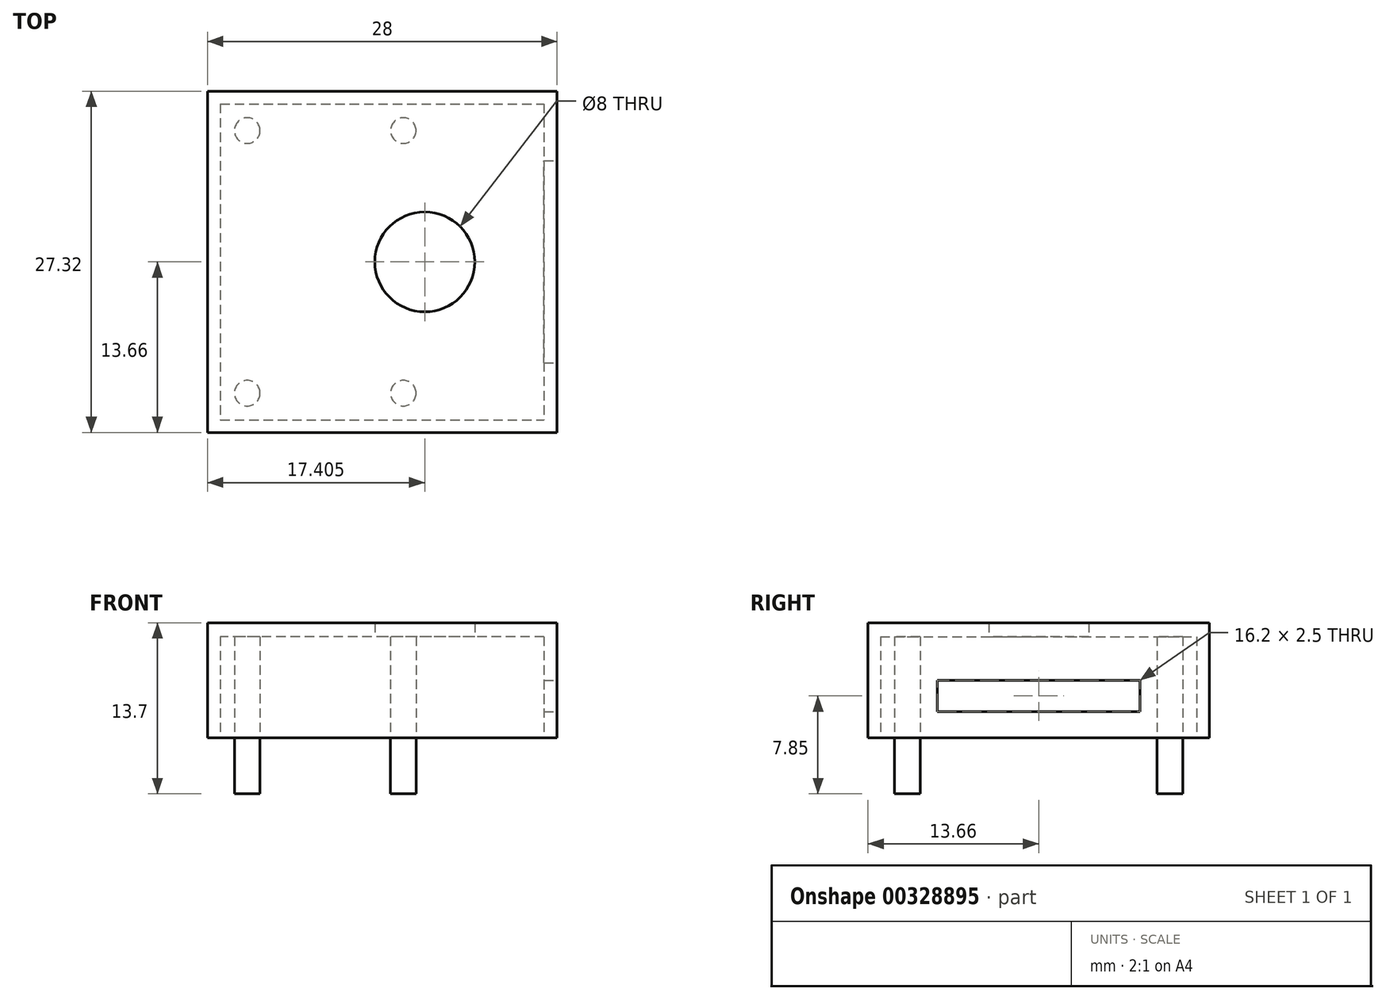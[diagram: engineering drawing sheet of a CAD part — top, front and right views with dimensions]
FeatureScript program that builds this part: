
annotation { "Feature Type Name" : "Feature", "Feature Type Description" : "" }
export const myFeature = defineFeature(function(context is Context, id is Id, definition is map)
    precondition{}
    {
        {
            var Q0;
            Q0=qCreatedBy(makeId("Top.planeOp"),FACE);
            var sketch = newSketch(context, id + "F0", { "sketchPlane" : qUnion([Q0])});
            skLineSegment(sketch, "E0.bottom", {"start": v(14, -13.66) * mm, "end": v(-14, -13.66) * mm});
            skLineSegment(sketch, "E0.top", {"start": v(14, 13.66) * mm, "end": v(-14, 13.66) * mm});
            skLineSegment(sketch, "E0.left", {"start": v(14, -13.66) * mm, "end": v(14, 13.66) * mm});
            skLineSegment(sketch, "E0.right", {"start": v(-14, -13.66) * mm, "end": v(-14, 13.66) * mm});
            skPoint(sketch, "E0.middle", {"position": v(0, 0) * mm});
            skLineSegment(sketch, "E1.bottom", {"start": v(12.96, -12.66) * mm, "end": v(-12.95, -12.66) * mm});
            skLineSegment(sketch, "E1.top", {"start": v(12.95, 12.66) * mm, "end": v(-12.96, 12.66) * mm});
            skLineSegment(sketch, "E1.left", {"start": v(12.96, -12.66) * mm, "end": v(12.95, 12.66) * mm});
            skLineSegment(sketch, "E1.right", {"start": v(-12.95, -12.66) * mm, "end": v(-12.96, 12.66) * mm});
            skCircle(sketch, "E2", {"center": v(-10.81, 10.51) * mm, "radius": 1.02 * mm});
            skCircle(sketch, "E3", {"center": v(1.69, 10.52) * mm, "radius": 1.02 * mm});
            skCircle(sketch, "E4", {"center": v(-10.8, -10.52) * mm, "radius": 1.02 * mm});
            skCircle(sketch, "E5", {"center": v(1.7, -10.52) * mm, "radius": 1.02 * mm});
            skLineSegment(sketch, "E6.bottom", {"start": v(7.46, -4.05) * mm, "end": v(-0.64, -4.05) * mm});
            skLineSegment(sketch, "E6.top", {"start": v(7.46, 4.05) * mm, "end": v(-0.64, 4.05) * mm});
            skLineSegment(sketch, "E6.left", {"start": v(7.46, -4.05) * mm, "end": v(7.45, 4.05) * mm});
            skLineSegment(sketch, "E6.right", {"start": v(-0.64, -4.05) * mm, "end": v(-0.64, 4.05) * mm});
            skPoint(sketch, "E6.middle", {"position": v(3.4, 0) * mm});
            skCircle(sketch, "E7", {"center": v(3.4, 0) * mm, "radius": 4 * mm});
            skSolve(sketch);
        }
        {
            var Q0;
            Q0=makeQuery(id+"F0.imprint","IMPRINT",FACE,{"disambiguationData":[TD([[makeQuery(id+"F0.imprint","IMPRINT",EDGE,{"derivedFrom":sQuery(id+"F0.wireOp",EDGE,"E1.bottom")}),-1.0]])]});
            var Q1;
            Q1=makeQuery(id+"F0.imprint","IMPRINT",FACE,{"disambiguationData":[TD([[makeQuery(id+"F0.imprint","IMPRINT",EDGE,{"derivedFrom":sQuery(id+"F0.wireOp",EDGE,"E3")}),1.0]])]});
            var Q2;
            Q2=makeQuery(id+"F0.imprint","IMPRINT",FACE,{"disambiguationData":[TD([[makeQuery(id+"F0.imprint","IMPRINT",EDGE,{"derivedFrom":sQuery(id+"F0.wireOp",EDGE,"E2")}),1.0]])]});
            var Q3;
            Q3=makeQuery(id+"F0.imprint","IMPRINT",FACE,{"disambiguationData":[TD([[makeQuery(id+"F0.imprint","IMPRINT",EDGE,{"derivedFrom":sQuery(id+"F0.wireOp",EDGE,"E5")}),1.0]])]});
            var Q4;
            Q4=makeQuery(id+"F0.imprint","IMPRINT",FACE,{"disambiguationData":[TD([[makeQuery(id+"F0.imprint","IMPRINT",EDGE,{"derivedFrom":sQuery(id+"F0.wireOp",EDGE,"E4")}),1.0]])]});
            var Q5;
            Q5=makeQuery(id+"F0.imprint","IMPRINT",FACE,{"disambiguationData":[TD([[makeQuery(id+"F0.imprint","IMPRINT",EDGE,{"derivedFrom":sQuery(id+"F0.wireOp",EDGE,"E0.bottom")}),-1.0]])]});
            var Q6;
            Q6=makeQuery(id+"F0.imprint","IMPRINT",FACE,{"disambiguationData":[TD([[makeQuery(id+"F0.imprint","IMPRINT",EDGE,{"derivedFrom":sQuery(id+"F0.wireOp",EDGE,"E6.bottom")}),-1.0]])]});
            extrude(context, id + "F1", {"entities" : qUnion([Q0, Q1, Q2, Q3, Q4, Q5, Q6]), "depth" : 9.2 * mm});
        }
        {
            var Q0;
            Q0=makeQuery(id+"F0.imprint","IMPRINT",FACE,{"disambiguationData":[TD([[makeQuery(id+"F0.imprint","IMPRINT",EDGE,{"derivedFrom":sQuery(id+"F0.wireOp",EDGE,"E1.bottom")}),-1.0]])]});
            var Q1;
            Q1=makeQuery(id+"F0.imprint","IMPRINT",FACE,{"disambiguationData":[TD([[makeQuery(id+"F0.imprint","IMPRINT",EDGE,{"derivedFrom":sQuery(id+"F0.wireOp",EDGE,"E6.bottom")}),-1.0]])]});
            extrude(context, id + "F2", {"entities" : qUnion([Q0, Q1]), "operationType" : NewBodyOperationType.REMOVE, "depth" : 8.1 * mm, "hasSecondDirection" : true, "secondDirectionOppositeDirection" : true, "secondDirectionDepth" : 25 * mm});
        }
        {
            var Q0;
            Q0=makeQuery(id+"F2.boolean.opBoolean","SPLIT",FACE,{"disambiguationData":[TD([makeQuery(id+"F2.opExtrude","SWEPT_FACE",FACE,{"disambiguationData":[OSD([sQuery(id+"F0.wireOp",EDGE,"E2")])]})])],"derivedFrom":makeQuery(id+"F1.opExtrude","CAP_FACE",FACE,{"disambiguationData":[OSD([sQuery(id+"F0.wireOp",EDGE,"E0.bottom"),sQuery(id+"F0.wireOp",EDGE,"E0.top"),sQuery(id+"F0.wireOp",EDGE,"E0.left"),sQuery(id+"F0.wireOp",EDGE,"E0.right"),sQuery(id+"F0.wireOp",EDGE,"E7")])],"isStart":true})});
            var Q1;
            Q1=makeQuery(id+"F2.boolean.opBoolean","SPLIT",FACE,{"disambiguationData":[TD([makeQuery(id+"F2.opExtrude","SWEPT_FACE",FACE,{"disambiguationData":[OSD([sQuery(id+"F0.wireOp",EDGE,"E4")])]})])],"derivedFrom":makeQuery(id+"F1.opExtrude","CAP_FACE",FACE,{"disambiguationData":[OSD([sQuery(id+"F0.wireOp",EDGE,"E0.bottom"),sQuery(id+"F0.wireOp",EDGE,"E0.top"),sQuery(id+"F0.wireOp",EDGE,"E0.left"),sQuery(id+"F0.wireOp",EDGE,"E0.right"),sQuery(id+"F0.wireOp",EDGE,"E7")])],"isStart":true})});
            var Q2;
            Q2=makeQuery(id+"F2.boolean.opBoolean","SPLIT",FACE,{"disambiguationData":[TD([makeQuery(id+"F2.opExtrude","SWEPT_FACE",FACE,{"disambiguationData":[OSD([sQuery(id+"F0.wireOp",EDGE,"E3")])]})])],"derivedFrom":makeQuery(id+"F1.opExtrude","CAP_FACE",FACE,{"disambiguationData":[OSD([sQuery(id+"F0.wireOp",EDGE,"E0.bottom"),sQuery(id+"F0.wireOp",EDGE,"E0.top"),sQuery(id+"F0.wireOp",EDGE,"E0.left"),sQuery(id+"F0.wireOp",EDGE,"E0.right"),sQuery(id+"F0.wireOp",EDGE,"E7")])],"isStart":true})});
            var Q3;
            Q3=makeQuery(id+"F2.boolean.opBoolean","SPLIT",FACE,{"disambiguationData":[TD([makeQuery(id+"F2.opExtrude","SWEPT_FACE",FACE,{"disambiguationData":[OSD([sQuery(id+"F0.wireOp",EDGE,"E5")])]})])],"derivedFrom":makeQuery(id+"F1.opExtrude","CAP_FACE",FACE,{"disambiguationData":[OSD([sQuery(id+"F0.wireOp",EDGE,"E0.bottom"),sQuery(id+"F0.wireOp",EDGE,"E0.top"),sQuery(id+"F0.wireOp",EDGE,"E0.left"),sQuery(id+"F0.wireOp",EDGE,"E0.right"),sQuery(id+"F0.wireOp",EDGE,"E7")])],"isStart":true})});
            extrude(context, id + "F3", {"entities" : qUnion([Q0, Q1, Q2, Q3]), "operationType" : NewBodyOperationType.ADD, "oppositeDirection" : true, "depth" : 0 * mm, "hasSecondDirection" : true, "secondDirectionOppositeDirection" : false, "secondDirectionDepth" : 4.5 * mm});
        }
        {
            var Q0;
            Q0=makeQuery(id+"F1.opExtrude","SWEPT_FACE",FACE,{"disambiguationData":[OSD([sQuery(id+"F0.wireOp",EDGE,"E0.left")])]});
            var sketch = newSketch(context, id + "F4", { "sketchPlane" : qUnion([Q0])});
            skLineSegment(sketch, "E8.bottom", {"start": v(8.1, 2.1) * mm, "end": v(-8.1, 2.1) * mm});
            skLineSegment(sketch, "E8.top", {"start": v(8.1, 4.6) * mm, "end": v(-8.1, 4.6) * mm});
            skLineSegment(sketch, "E8.left", {"start": v(8.1, 2.1) * mm, "end": v(8.1, 4.6) * mm});
            skLineSegment(sketch, "E8.right", {"start": v(-8.1, 2.1) * mm, "end": v(-8.1, 4.6) * mm});
            skPoint(sketch, "E8.middle", {"position": v(0, 3.35) * mm});
            skSolve(sketch);
        }
        {
            var Q0;
            Q0 = qSketchRegion(id + "F4", true);
            extrude(context, id + "F5", {"entities" : qUnion([Q0]), "operationType" : NewBodyOperationType.REMOVE, "oppositeDirection" : true, "depth" : 5 * mm});
        }
    });
